# Revit family: rondel_flat_0md5307l1840
name_source: partatom
category: Lighting Fixtures
units: mm (PartAtom-declared; Revit-internal decimal feet)

## family parameters
Cut with Voids When Loaded = No
Host = Face
Light Source = No
Part Type = Normal
Room Calculation Point = No
Round Connector Dimension = Use Diameter
Shared = No

## types (1)
- RONDEL Flat (1 x LED 4000K / CRI = 80 (unbekannt), 1800 lm, 4000K)
    Apparent Load = 18 VA
    CIE Flux Codes = 43 74 92 91 100
    Color Rendering = 80
    Color Temperature = 4000K
    Default Elevation = 1800 mm  [stored 5.90551 ft]
    Description = RONDEL Flat, wall and ceiling luminaire, of PC, opal, light emission: direct distribution, installation type: surface-mounted, LED, rated luminous flux: 1.800lm, luminous efficacy: 100lm/W, light colour: 840, colour temperature: 4000K, control gear: ON/OFF, with terminal, 2-pole, mains connection: 220..240V, AC, 50/60Hz, rated input power: 18W, housing, round, of sheet steel, powder-coated, white, diameter: 380mm, height: 28mm, cover, of PC, graphite (RAL 7037), protection rating (complete): IP40, insulation class (complete): insulation class II (safety insulation), certification: CE, impact resistance: IK03, permissible operating ambient temperature: -20..+40°C, permissible storage temperature: -20..+80°C, packaging unit: 1 piece
    Height = 28 mm
    Lamp = 1 x LED 4000K / CRI >= 80 (unbekannt)
    Lamp Light Flux = 1800 lm
    Lamp count = 1
    Length = 380 mm
    Luminous efficacy = 100 lm/W
    Manufacturer = Siteco
    ModVariant = No
    Model = 0MD5307L1840
    Mounting Place = Ceiling
    Mounting Type = Surface mounted
    Number of Poles = 1
    OnlyDefault = Yes
    Power Factor = 1
    Product Name = RONDEL Flat
    Product group = wall and ceiling luminaire
    ProductGroupID = 304
    Protection Class = Protection class II
    Protection Degree = IP 40
    RLX_Detail_Level = 1
    RLX_Emergency_Light_Flux = 0 lm
    RLX_Emergency_Type = 0
    RLX_Emergency_Type_DB = No
    RlxData = <blob elided: 49533 chars, md5=c0ac46aa>
    Socket = socket
    Standby Power = 0 W
    System Light Flux = 1800 lm
    System Power = 18 W
    Type Comments = Product without accessories
    Type Image = l_1005688.jpg
    URL = http://relux.com
    VarID = ---
    Voltage = 0 V
    Weight = 0.00 kg
    Width = 0 mm  [stored 0 ft]

note: [stored X ft] marks values corroborated as IEEE doubles in the binary element streams (Revit-internal decimal feet)

## geometry (parser evidence)
native form markers: Sweep x15
no freeform markers — native parametric forms only
